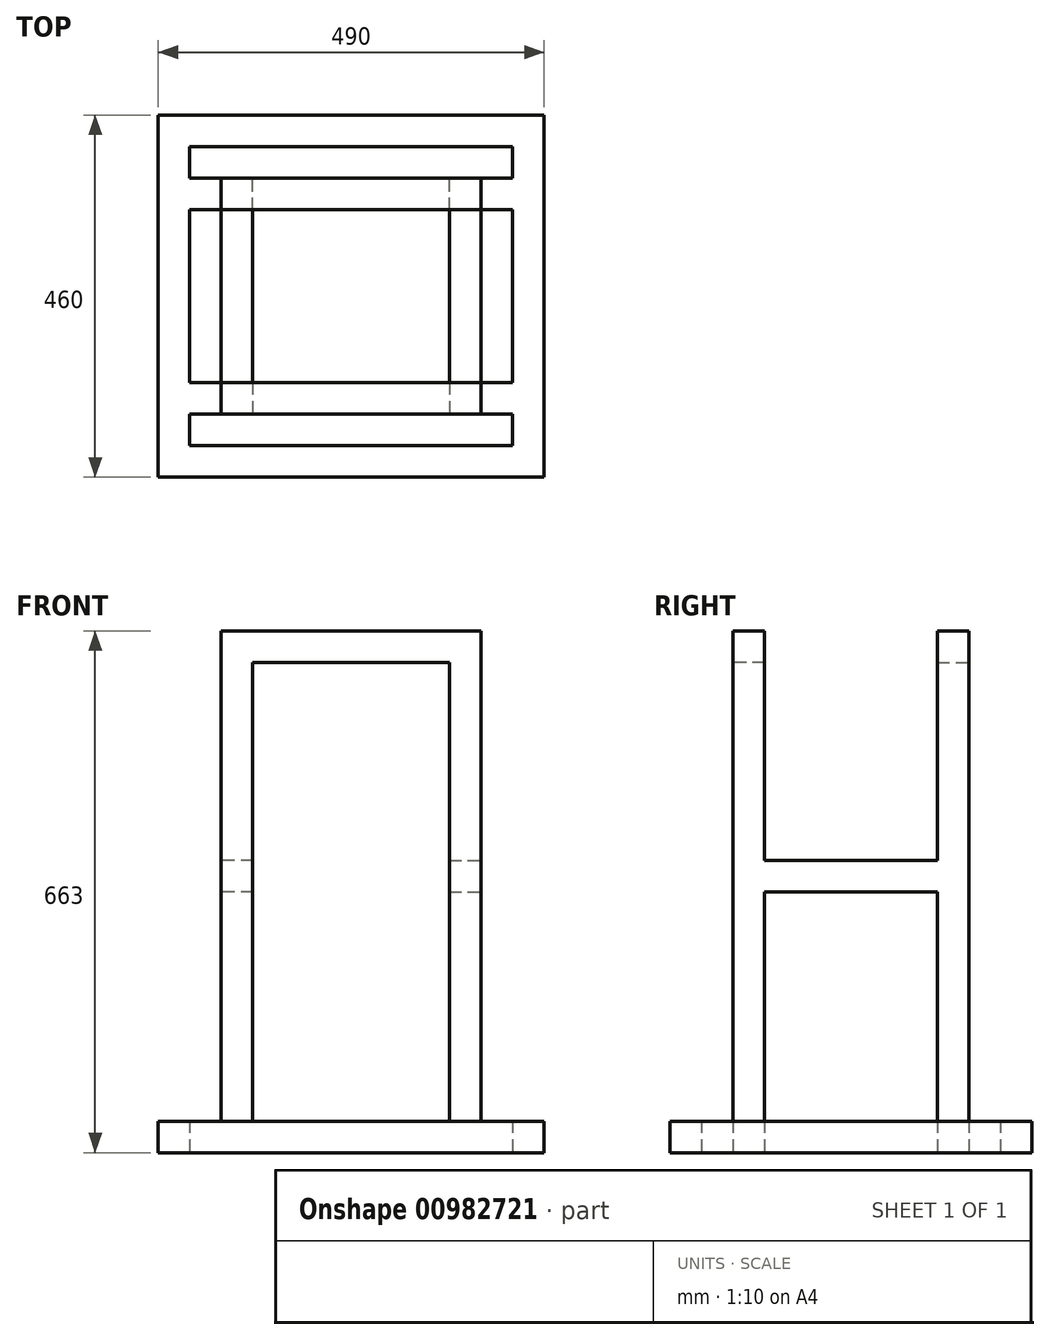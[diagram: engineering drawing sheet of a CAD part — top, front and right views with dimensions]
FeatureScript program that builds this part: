
annotation { "Feature Type Name" : "Feature", "Feature Type Description" : "" }
export const myFeature = defineFeature(function(context is Context, id is Id, definition is map)
    precondition{}
    {
        {
            var Q0;
            Q0=qCreatedBy(makeId("Top.planeOp"),FACE);
            var sketch = newSketch(context, id + "F0", { "sketchPlane" : qUnion([Q0])});
            skLineSegment(sketch, "E0.bottom", {"start": v(245, -230) * mm, "end": v(-245, -230) * mm});
            skLineSegment(sketch, "E0.top", {"start": v(245, 230) * mm, "end": v(-245, 230) * mm});
            skLineSegment(sketch, "E0.left", {"start": v(245, -230) * mm, "end": v(245, 230) * mm});
            skLineSegment(sketch, "E0.right", {"start": v(-245, -230) * mm, "end": v(-245, 230) * mm});
            skPoint(sketch, "E0.middle", {"position": v(0, 0) * mm});
            skLineSegment(sketch, "E1.bottom", {"start": v(205, -190) * mm, "end": v(-205, -190) * mm});
            skLineSegment(sketch, "E1.top", {"start": v(205, 190) * mm, "end": v(-205, 190) * mm});
            skLineSegment(sketch, "E1.left", {"start": v(205, -190) * mm, "end": v(205, 190) * mm});
            skLineSegment(sketch, "E1.right", {"start": v(-205, -190) * mm, "end": v(-205, 190) * mm});
            skLineSegment(sketch, "E2.bottom", {"start": v(205, -150) * mm, "end": v(-205, -150) * mm});
            skLineSegment(sketch, "E2.top", {"start": v(205, -110) * mm, "end": v(-205, -110) * mm});
            skLineSegment(sketch, "E2.left", {"start": v(205, -150) * mm, "end": v(205, -110) * mm});
            skLineSegment(sketch, "E2.right", {"start": v(-205, -150) * mm, "end": v(-205, -110) * mm});
            skPoint(sketch, "E2.middle", {"position": v(0, -130) * mm});
            skLineSegment(sketch, "E3.bottom", {"start": v(205, 110) * mm, "end": v(-205, 110) * mm});
            skLineSegment(sketch, "E3.top", {"start": v(205, 150) * mm, "end": v(-205, 150) * mm});
            skLineSegment(sketch, "E3.left", {"start": v(205, 110) * mm, "end": v(205, 150) * mm});
            skLineSegment(sketch, "E3.right", {"start": v(-205, 110) * mm, "end": v(-205, 150) * mm});
            skPoint(sketch, "E3.middle", {"position": v(0, 130) * mm});
            skSolve(sketch);
        }
        {
            var Q0;
            Q0=makeQuery(id+"F0.imprint","IMPRINT",FACE,{"disambiguationData":[TD([[makeQuery(id+"F0.imprint","IMPRINT",EDGE,{"derivedFrom":sQuery(id+"F0.wireOp",EDGE,"E3.bottom")}),-1.0]])]});
            var Q1;
            Q1=makeQuery(id+"F0.imprint","IMPRINT",FACE,{"disambiguationData":[TD([[makeQuery(id+"F0.imprint","IMPRINT",EDGE,{"derivedFrom":sQuery(id+"F0.wireOp",EDGE,"E0.bottom")}),-1.0]])]});
            var Q2;
            Q2=makeQuery(id+"F0.imprint","IMPRINT",FACE,{"disambiguationData":[TD([[makeQuery(id+"F0.imprint","IMPRINT",EDGE,{"derivedFrom":sQuery(id+"F0.wireOp",EDGE,"E2.bottom")}),-1.0]])]});
            extrude(context, id + "F1", {"entities" : qUnion([Q0, Q1, Q2]), "depth" : 40 * mm, "offsetDistance" : 25 * mm});
        }
        {
            var Q0;
            Q0=makeQuery(id+"F1.opExtrude","CAP_FACE",FACE,{"disambiguationData":[OSD([sQuery(id+"F0.wireOp",EDGE,"E0.bottom"),sQuery(id+"F0.wireOp",EDGE,"E0.top"),sQuery(id+"F0.wireOp",EDGE,"E0.left"),sQuery(id+"F0.wireOp",EDGE,"E0.right"),sQuery(id+"F0.wireOp",EDGE,"E1.bottom"),sQuery(id+"F0.wireOp",EDGE,"E1.top"),sQuery(id+"F0.wireOp",EDGE,"E1.left"),sQuery(id+"F0.wireOp",EDGE,"E1.right"),sQuery(id+"F0.wireOp",EDGE,"E2.bottom"),sQuery(id+"F0.wireOp",EDGE,"E2.top"),sQuery(id+"F0.wireOp",EDGE,"E3.bottom"),sQuery(id+"F0.wireOp",EDGE,"E3.top")])],"isStart":false});
            var sketch = newSketch(context, id + "F2", { "sketchPlane" : qUnion([Q0])});
            skLineSegment(sketch, "E4.bottom", {"start": v(-125, 110) * mm, "end": v(-165, 110) * mm});
            skLineSegment(sketch, "E4.top", {"start": v(-125, 150) * mm, "end": v(-165, 150) * mm});
            skLineSegment(sketch, "E4.left", {"start": v(-125, 110) * mm, "end": v(-125, 150) * mm});
            skLineSegment(sketch, "E4.right", {"start": v(-165, 110) * mm, "end": v(-165, 150) * mm});
            skPoint(sketch, "E4.middle", {"position": v(-145, 130) * mm});
            skLineSegment(sketch, "E5.MirrorCS", {"start": v(-165, -110) * mm, "end": v(-165, -150) * mm});
            skLineSegment(sketch, "E6.MirrorCS", {"start": v(-125, -150) * mm, "end": v(-165, -150) * mm});
            skLineSegment(sketch, "E7.MirrorCS", {"start": v(-125, -110) * mm, "end": v(-125, -150) * mm});
            skLineSegment(sketch, "E8.MirrorCS", {"start": v(-125, -110) * mm, "end": v(-165, -110) * mm});
            skLineSegment(sketch, "E9.MirrorCS", {"start": v(125, 110) * mm, "end": v(125, 150) * mm});
            skLineSegment(sketch, "E10.MirrorCS", {"start": v(125, 150) * mm, "end": v(165, 150) * mm});
            skLineSegment(sketch, "E11.MirrorCS", {"start": v(165, 110) * mm, "end": v(165, 150) * mm});
            skLineSegment(sketch, "E12.MirrorCS", {"start": v(125, 110) * mm, "end": v(165, 110) * mm});
            skLineSegment(sketch, "E13.MirrorCS", {"start": v(125, -110) * mm, "end": v(165, -110) * mm});
            skLineSegment(sketch, "E14.MirrorCS", {"start": v(165, -110) * mm, "end": v(165, -150) * mm});
            skLineSegment(sketch, "E15.MirrorCS", {"start": v(125, -150) * mm, "end": v(165, -150) * mm});
            skLineSegment(sketch, "E16.MirrorCS", {"start": v(125, -110) * mm, "end": v(125, -150) * mm});
            skSolve(sketch);
        }
        {
            var Q0;
            Q0=makeQuery(id+"F2.imprint","IMPRINT",FACE,{"disambiguationData":[TD([[makeQuery(id+"F2.imprint","IMPRINT",EDGE,{"derivedFrom":sQuery(id+"F2.wireOp",EDGE,"E4.bottom")}),-1.0]])]});
            var Q1;
            Q1=makeQuery(id+"F2.imprint","IMPRINT",FACE,{"disambiguationData":[TD([[makeQuery(id+"F2.imprint","IMPRINT",EDGE,{"derivedFrom":sQuery(id+"F2.wireOp",EDGE,"E9.MirrorCS")}),-1.0]])]});
            var Q2;
            Q2=makeQuery(id+"F2.imprint","IMPRINT",FACE,{"disambiguationData":[TD([[makeQuery(id+"F2.imprint","IMPRINT",EDGE,{"derivedFrom":sQuery(id+"F2.wireOp",EDGE,"E13.MirrorCS")}),1.0]])]});
            var Q3;
            Q3=makeQuery(id+"F2.imprint","IMPRINT",FACE,{"disambiguationData":[TD([[makeQuery(id+"F2.imprint","IMPRINT",EDGE,{"derivedFrom":sQuery(id+"F2.wireOp",EDGE,"E5.MirrorCS")}),1.0]])]});
            extrude(context, id + "F3", {"entities" : qUnion([Q0, Q1, Q2, Q3]), "operationType" : NewBodyOperationType.ADD, "depth" : 623 * mm, "offsetDistance" : 25 * mm});
        }
        {
            var Q0;
            Q0=makeQuery(id+"F3.opExtrude","CAP_FACE",FACE,{"disambiguationData":[OSD([sQuery(id+"F2.wireOp",EDGE,"E9.MirrorCS"),sQuery(id+"F2.wireOp",EDGE,"E10.MirrorCS"),sQuery(id+"F2.wireOp",EDGE,"E11.MirrorCS"),sQuery(id+"F2.wireOp",EDGE,"E12.MirrorCS")])],"isStart":false});
            var sketch = newSketch(context, id + "F4", { "sketchPlane" : qUnion([Q0])});
            skLineSegment(sketch, "E17.bottom", {"start": v(165, 150) * mm, "end": v(-165, 150) * mm});
            skLineSegment(sketch, "E17.top", {"start": v(165, 110) * mm, "end": v(-165, 110) * mm});
            skLineSegment(sketch, "E17.left", {"start": v(165, 150) * mm, "end": v(165, 110) * mm});
            skLineSegment(sketch, "E17.right", {"start": v(-165, 150) * mm, "end": v(-165, 110) * mm});
            skLineSegment(sketch, "E18.bottom", {"start": v(165, -150) * mm, "end": v(-165, -150) * mm});
            skLineSegment(sketch, "E18.top", {"start": v(165, -110) * mm, "end": v(-165, -110) * mm});
            skLineSegment(sketch, "E18.left", {"start": v(165, -150) * mm, "end": v(165, -110) * mm});
            skLineSegment(sketch, "E18.right", {"start": v(-165, -150) * mm, "end": v(-165, -110) * mm});
            skSolve(sketch);
        }
        {
            var Q0;
            {var subQ2=sQuery(id+"F4.wireOp",EDGE,"E17.right");Q0=makeQuery(id+"F4.imprint","IMPRINT",FACE,{"disambiguationData":[TD([[makeQuery(id+"F4.imprint","IMPRINT",EDGE,{"derivedFrom":subQ2}),1.0]])]});}
            var Q1;
            Q1=makeQuery(id+"F4.imprint","IMPRINT",FACE,{"disambiguationData":[TD([[makeQuery(id+"F4.imprint","IMPRINT",EDGE,{"derivedFrom":sQuery(id+"F4.wireOp",EDGE,"E18.bottom")}),-1.0]])]});
            extrude(context, id + "F5", {"entities" : qUnion([Q0, Q1]), "operationType" : NewBodyOperationType.ADD, "oppositeDirection" : true, "depth" : 40 * mm, "offsetDistance" : 25 * mm});
        }
        {
            var Q0;
            Q0=makeQuery(id+"F3.opExtrude","SWEPT_FACE",FACE,{"disambiguationData":[OSD([sQuery(id+"F2.wireOp",EDGE,"E14.MirrorCS")])]});
            var sketch = newSketch(context, id + "F6", { "sketchPlane" : qUnion([Q0])});
            skLineSegment(sketch, "E19.bottom", {"start": v(110, 331.5) * mm, "end": v(-110, 331.5) * mm});
            skLineSegment(sketch, "E19.top", {"start": v(110, 371.5) * mm, "end": v(-110, 371.5) * mm});
            skLineSegment(sketch, "E19.left", {"start": v(110, 331.5) * mm, "end": v(110, 371.5) * mm});
            skLineSegment(sketch, "E19.right", {"start": v(-110, 331.5) * mm, "end": v(-110, 371.5) * mm});
            skPoint(sketch, "E19.middle", {"position": v(0, 351.5) * mm});
            skPoint(sketch, "E19.middle.positionSnap0", {"position": v(-110, 351.5) * mm});
            skPoint(sketch, "E19.centerSnap0", {"position": v(-110, 351.5) * mm});
            skSolve(sketch);
        }
        {
            var Q0;
            Q0=makeQuery(id+"F6.imprint","IMPRINT",FACE,{"disambiguationData":[TD([[makeQuery(id+"F6.imprint","IMPRINT",EDGE,{"derivedFrom":sQuery(id+"F6.wireOp",EDGE,"E19.bottom")}),-1.0]])]});
            extrude(context, id + "F7", {"entities" : qUnion([Q0]), "operationType" : NewBodyOperationType.ADD, "oppositeDirection" : true, "depth" : 40 * mm, "offsetDistance" : 25 * mm});
        }
        {
            var Q0;
            Q0=makeQuery(id+"F3.opExtrude","SWEPT_FACE",FACE,{"disambiguationData":[OSD([sQuery(id+"F2.wireOp",EDGE,"E4.right")])]});
            var sketch = newSketch(context, id + "F8", { "sketchPlane" : qUnion([Q0])});
            skLineSegment(sketch, "E20.bottom", {"start": v(110, 331.5) * mm, "end": v(-110, 331.5) * mm});
            skLineSegment(sketch, "E20.top", {"start": v(110, 371.5) * mm, "end": v(-110, 371.5) * mm});
            skLineSegment(sketch, "E20.left", {"start": v(110, 331.5) * mm, "end": v(110, 371.5) * mm});
            skLineSegment(sketch, "E20.right", {"start": v(-110, 331.5) * mm, "end": v(-110, 371.5) * mm});
            skPoint(sketch, "E20.middle", {"position": v(0, 351.5) * mm});
            skPoint(sketch, "E20.middle.positionSnap0", {"position": v(-110, 351.5) * mm});
            skPoint(sketch, "E20.centerSnap0", {"position": v(-110, 351.5) * mm});
            skSolve(sketch);
        }
        {
            var Q0;
            Q0=makeQuery(id+"F8.imprint","IMPRINT",FACE,{"disambiguationData":[TD([[makeQuery(id+"F8.imprint","IMPRINT",EDGE,{"derivedFrom":sQuery(id+"F8.wireOp",EDGE,"E20.bottom")}),-1.0]])]});
            extrude(context, id + "F9", {"entities" : qUnion([Q0]), "operationType" : NewBodyOperationType.ADD, "oppositeDirection" : true, "depth" : 40 * mm, "offsetDistance" : 25 * mm});
        }
    });
